# Revit family: CL-115
name_source: partatom
category: Plumbing Fixtures
revit_build: Autodesk Revit Architecture 2012 (Build: 20110309_2315(x64)
units: mm (PartAtom-declared; Revit-internal decimal feet)

## types (1)
- CL-115
    Assembly Code = D2010
    Basin spout = CL-066SQPT210
    CW Connection = Yes
    CWFU = 0
    Cost = 0 $
    Default Elevation = 0' - 0"
    Description = Two hole with pillar spout + sidevalve 1/2"BSP male inlet
    HW Connection = Yes
    HWFU = 0
    Headpart clockwise closing = S-21-1CLOCK
    Keynote = 1 x 350mm spout flexible connection for wide range of centre distances
    Manufacturer = COBRA
    Material = Chrome - Polished
    Model = CL-115
    Range = Callisto
    Side body to spout connection hoses = C-15/350
    Type Comments = SANS 226 type 1
    URL = http://www.cobra.co.za
    Vent Connection = No
    WFU = 0
    Waste Connection = No

## geometry (parser evidence)
native form markers: Blend x2
no freeform markers — native parametric forms only
